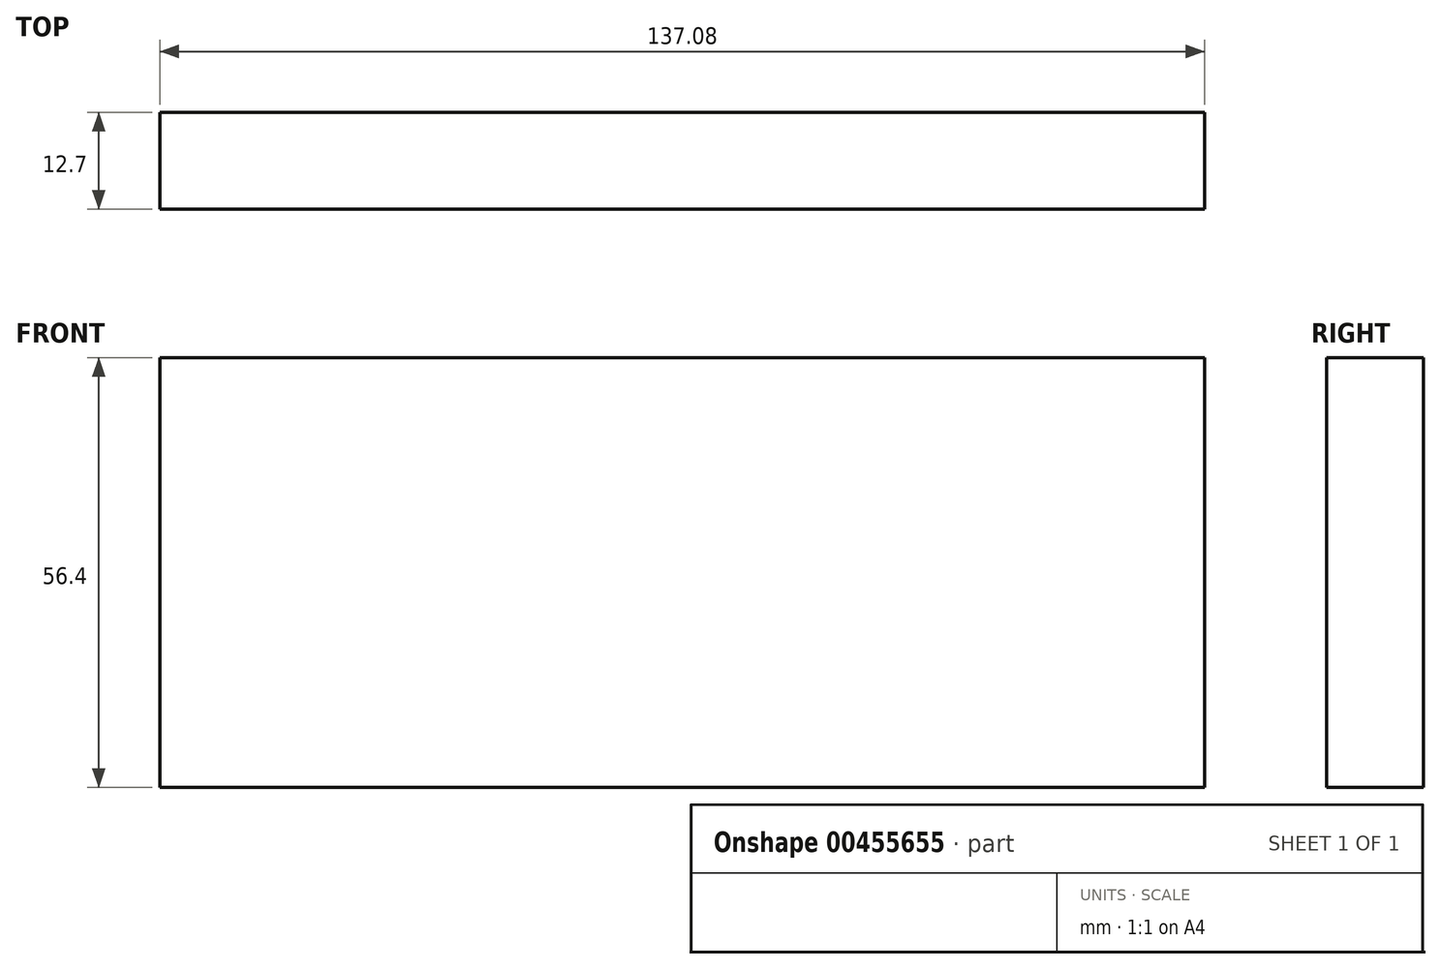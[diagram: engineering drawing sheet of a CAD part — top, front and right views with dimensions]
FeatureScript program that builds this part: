
annotation { "Feature Type Name" : "Feature", "Feature Type Description" : "" }
export const myFeature = defineFeature(function(context is Context, id is Id, definition is map)
    precondition{}
    {
        {
            var Q0;
            Q0=qCreatedBy(makeId("Front.planeOp"),FACE);
            var sketch = newSketch(context, id + "F0", { "sketchPlane" : qUnion([Q0])});
            skLineSegment(sketch, "E0.bottom", {"start": v(68.54, 28.2) * mm, "end": v(-68.54, 28.2) * mm});
            skLineSegment(sketch, "E0.top", {"start": v(68.54, -28.2) * mm, "end": v(-68.54, -28.2) * mm});
            skLineSegment(sketch, "E0.left", {"start": v(68.54, 28.2) * mm, "end": v(68.54, -28.2) * mm});
            skLineSegment(sketch, "E0.right", {"start": v(-68.54, 28.2) * mm, "end": v(-68.54, -28.2) * mm});
            skPoint(sketch, "E0.middle", {"position": v(0, 0) * mm});
            skSolve(sketch);
        }
        {
            var Q0;
            Q0 = qSketchRegion(id + "F0", true);
            extrude(context, id + "F1", {"entities" : qUnion([Q0]), "depth" : 12.7 * mm});
        }
    });
